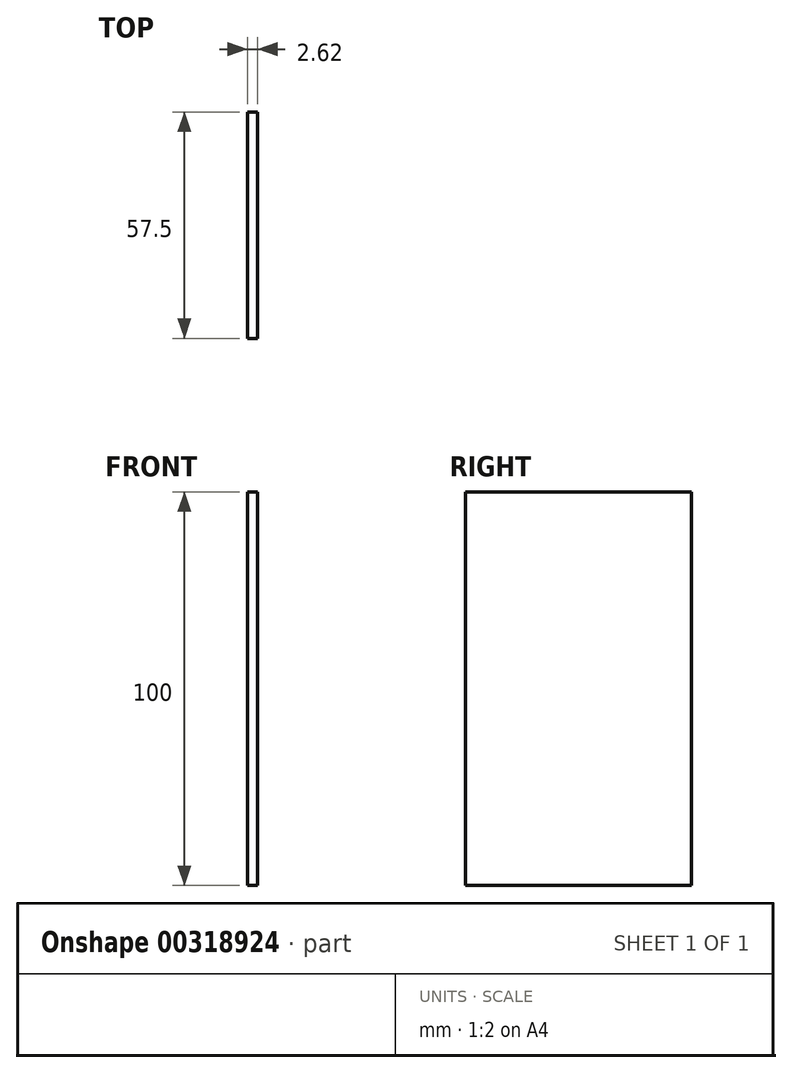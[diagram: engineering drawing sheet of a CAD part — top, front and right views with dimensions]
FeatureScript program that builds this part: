
annotation { "Feature Type Name" : "Feature", "Feature Type Description" : "" }
export const myFeature = defineFeature(function(context is Context, id is Id, definition is map)
    precondition{}
    {
        {
            var Q0;
            Q0=qCreatedBy(makeId("Right.planeOp"),FACE);
            var sketch = newSketch(context, id + "F0", { "sketchPlane" : qUnion([Q0])});
            skLineSegment(sketch, "E0.bottom", {"start": v(28.75, -50) * mm, "end": v(-28.75, -50) * mm});
            skLineSegment(sketch, "E0.top", {"start": v(28.75, 50) * mm, "end": v(-28.75, 50) * mm});
            skLineSegment(sketch, "E0.left", {"start": v(28.75, -50) * mm, "end": v(28.75, 50) * mm});
            skLineSegment(sketch, "E0.right", {"start": v(-28.75, -50) * mm, "end": v(-28.75, 50) * mm});
            skPoint(sketch, "E0.middle", {"position": v(0, 0) * mm});
            skSolve(sketch);
        }
        {
            var Q0;
            Q0=makeQuery(id+"F0.imprint","IMPRINT",FACE,{"disambiguationData":[TD([[makeQuery(id+"F0.imprint","IMPRINT",EDGE,{"derivedFrom":sQuery(id+"F0.wireOp",EDGE,"E0.bottom")}),-1.0]])]});
            extrude(context, id + "F1", {"entities" : qUnion([Q0]), "depth" : 2.62 * mm});
        }
    });
